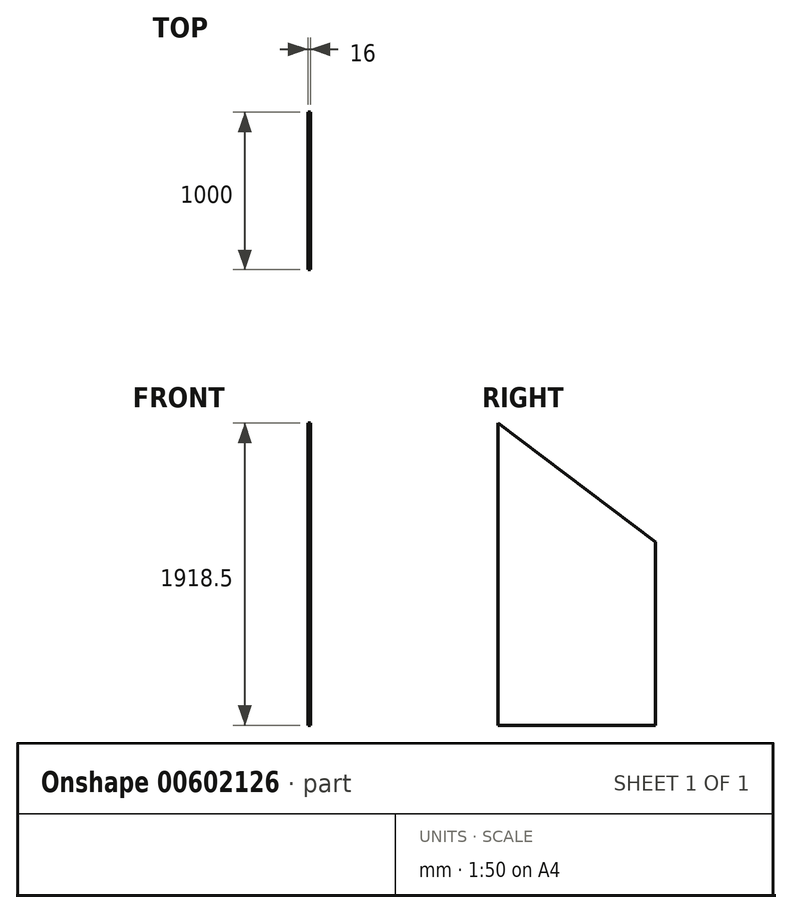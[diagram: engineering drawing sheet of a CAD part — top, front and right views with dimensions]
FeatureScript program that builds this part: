
annotation { "Feature Type Name" : "Feature", "Feature Type Description" : "" }
export const myFeature = defineFeature(function(context is Context, id is Id, definition is map)
    precondition{}
    {
        {
            var Q0;
            Q0=qCreatedBy(makeId("Right.planeOp"),FACE);
            var sketch = newSketch(context, id + "F0", { "sketchPlane" : qUnion([Q0])});
            skLineSegment(sketch, "E0", {"start": v(-1000, 1918.5) * mm, "end": v(-1000, 0) * mm});
            skLineSegment(sketch, "E1", {"start": v(-1000, 0) * mm, "end": v(0, 0) * mm});
            skLineSegment(sketch, "E2", {"start": v(0, 0) * mm, "end": v(0, 1164.95) * mm});
            skLineSegment(sketch, "E3", {"start": v(0, 1164.95) * mm, "end": v(-1000, 1918.5) * mm});
            skSolve(sketch);
        }
        {
            var Q0;
            Q0 = qSketchRegion(id + "F0", true);
            extrude(context, id + "F1", {"entities" : qUnion([Q0]), "depth" : 16 * mm, "offsetDistance" : 25 * mm});
        }
    });
